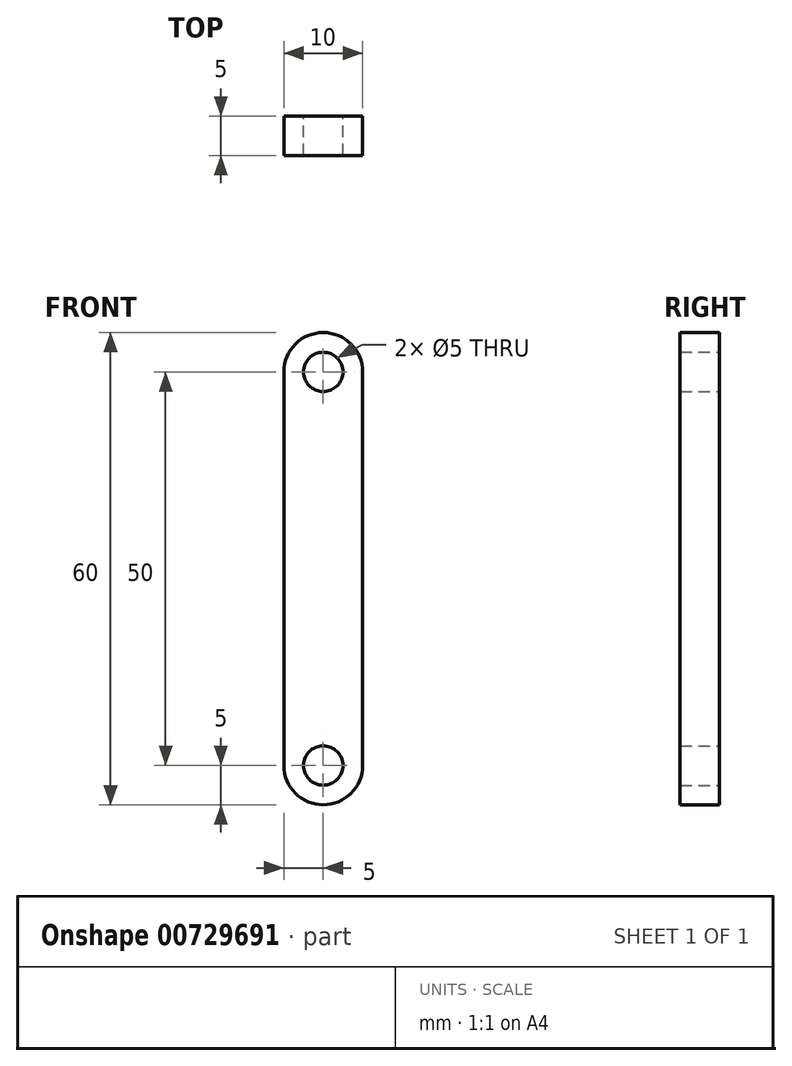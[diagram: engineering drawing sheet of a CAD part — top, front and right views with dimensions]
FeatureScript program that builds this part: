
annotation { "Feature Type Name" : "Feature", "Feature Type Description" : "" }
export const myFeature = defineFeature(function(context is Context, id is Id, definition is map)
    precondition{}
    {
        {
            var Q0;
            Q0=qCreatedBy(makeId("Front.planeOp"),FACE);
            var sketch = newSketch(context, id + "F0", { "sketchPlane" : qUnion([Q0])});
            skArc(sketch, "E0", {"start": v(5, 25) * mm, "mid": v(0, 30) * mm, "end": v(-5, 25) * mm});
            skArc(sketch, "E1", {"start": v(-5, -25) * mm, "mid": v(0, -30) * mm, "end": v(5, -25) * mm});
            skCircle(sketch, "E2", {"center": v(0, 25) * mm, "radius": 2.5 * mm});
            skCircle(sketch, "E3", {"center": v(0, -25) * mm, "radius": 2.5 * mm});
            skLineSegment(sketch, "E4", {"start": v(-5, 25) * mm, "end": v(-5, -25) * mm});
            skLineSegment(sketch, "E5", {"start": v(5, 25) * mm, "end": v(5, -25) * mm});
            skSolve(sketch);
        }
        {
            var Q0;
            Q0=makeQuery(id+"F0.imprint","IMPRINT",FACE,{"disambiguationData":[TD([[makeQuery(id+"F0.imprint","IMPRINT",EDGE,{"derivedFrom":sQuery(id+"F0.wireOp",EDGE,"E0")}),1.0]])]});
            extrude(context, id + "F1", {"entities" : qUnion([Q0]), "endBound" : BoundingType.SYMMETRIC, "depth" : 5 * mm, "offsetDistance" : 25 * mm});
        }
    });
